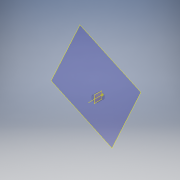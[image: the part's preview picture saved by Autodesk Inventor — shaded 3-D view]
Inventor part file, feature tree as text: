
AUTODESK INVENTOR PART (.ipt)
format: ipt  version: 2019 (Build 230136000, 136)  size: 115,200 bytes
history: native  units: mm
features: other x7, plane x3, reference x3, sketch x1, extrude x1
ambient origin geometry x8: Origin, YZ Plane, XZ Plane, XY Plane, X Axis, Y Axis, Z Axis, Center Point
bodies: Solid1 (feature_tree)
feature tree (15):
  plane  "Work Plane1"
  sketch  "Sketch1"  dims[d0=10.5mm d1=11.0mm d2=10.5mm d3=5.0mm d4=10.0mm d5=0.0mm]
  other  "Work Point1"
  extrude  "Extrusion1"  Depth=10.0mm
  plane  "Arbeitsebene3"
  reference  "Reference1"
  reference  "Reference2"
  reference  "Reference3"
  other  "Arbeitsachse1"
  plane  "Arbeitsebene2"
  other  "Arbeitspunkt2"
  other  "<userpath>\Downloads\cellSTORM\00_KES400.iam"
  other  "00_KES400.iam"
  other  "00_KES_Bluray_Magnet:1"
  other  "00_KES400_Bluray_Lens:1"
